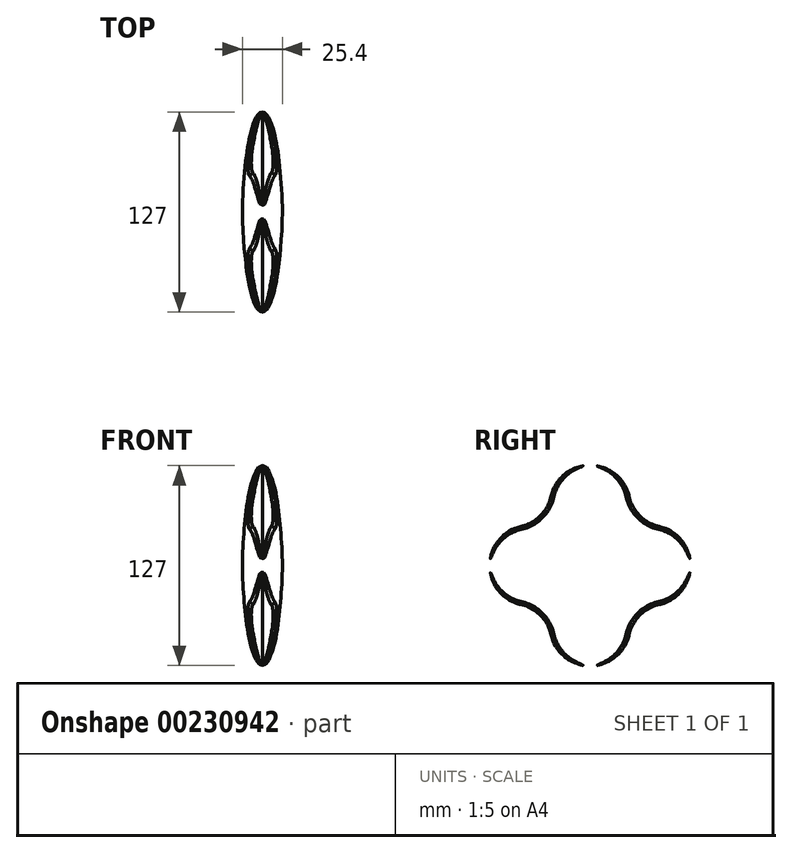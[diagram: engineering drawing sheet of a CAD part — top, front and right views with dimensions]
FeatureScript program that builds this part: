
annotation { "Feature Type Name" : "Feature", "Feature Type Description" : "" }
export const myFeature = defineFeature(function(context is Context, id is Id, definition is map)
    precondition{}
    {
        {
            var Q0;
            Q0=qCreatedBy(makeId("Top.planeOp"),FACE);
            var sketch = newSketch(context, id + "F0", { "sketchPlane" : qUnion([Q0])});
            skLineSegment(sketch, "E0", {"start": v(-58.3, 0) * mm, "end": v(61.26, 0) * mm, "construction": true});
            skLineSegment(sketch, "E1.bottom", {"start": v(0, 0) * mm, "end": v(-12.7, 0) * mm, "construction": true});
            skLineSegment(sketch, "E1.top", {"start": v(0, 63.5) * mm, "end": v(-12.7, 63.5) * mm, "construction": true});
            skLineSegment(sketch, "E1.left", {"start": v(0, 0) * mm, "end": v(0, 63.5) * mm, "construction": true});
            skLineSegment(sketch, "E1.right", {"start": v(-12.7, 0) * mm, "end": v(-12.7, 63.5) * mm, "construction": true});
            skPoint(sketch, "E2.2.internal.snap0", {"position": v(-6.35, 0) * mm});
            skFitSpline(sketch, "E2", {"points": [v(-12.7, 0) * mm, v(-10.15, 35.67) * mm, v(-6.35, 54.34) * mm, v(0, 63.5) * mm], "startDerivative": vector(0, 78.54) * mm, "endDerivative": vector(35.42, 0) * mm});
            skLineSegment(sketch, "E3", {"start": v(-12.7, 0) * mm, "end": v(0, 0) * mm});
            skLineSegment(sketch, "E4.MirrorCS", {"start": v(12.7, 0) * mm, "end": v(0, 0) * mm});
            skFitSpline(sketch, "E5.MirrorCS", {"points": [v(12.7, 0) * mm, v(10.15, 35.67) * mm, v(6.35, 54.34) * mm, v(0, 63.5) * mm], "startDerivative": vector(0, 78.54) * mm, "endDerivative": vector(-35.42, 0) * mm});
            skSolve(sketch);
        }
        {
            var Q0;
            Q0 = qSketchRegion(id + "F0", true);
            var Q1;
            Q1=sQuery(id+"F0.wireOp",EDGE,"E0");
            revolve(context, id + "F1", {"entities" : qUnion([Q0]), "axis" : qUnion([Q1]), "revolveType" : RevolveType.FULL});
        }
        {
            var Q0;
            Q0=qCreatedBy(makeId("Right.planeOp"),FACE);
            var sketch = newSketch(context, id + "F2", { "sketchPlane" : qUnion([Q0])});
            skLineSegment(sketch, "E6", {"start": v(68.88, 0) * mm, "end": v(-71.01, 0) * mm, "construction": true});
            skLineSegment(sketch, "E7", {"start": v(0, 73.64) * mm, "end": v(0, -72.57) * mm, "construction": true});
            skArc(sketch, "E8", {"start": v(43.95, -24.78) * mm, "mid": v(63.75, 0) * mm, "end": v(43.95, 24.78) * mm});
            skArc(sketch, "E9.1.0", {"start": v(24.78, 43.95) * mm, "mid": v(0, 63.75) * mm, "end": v(-24.78, 43.95) * mm});
            skArc(sketch, "E9.2.0", {"start": v(-43.95, 24.78) * mm, "mid": v(-63.75, 0) * mm, "end": v(-43.95, -24.78) * mm});
            skArc(sketch, "E9.3.0", {"start": v(-24.78, -43.95) * mm, "mid": v(0, -63.75) * mm, "end": v(24.78, -43.95) * mm});
            skPoint(sketch, "E9.center", {"position": v(0, 0) * mm});
            skArc(sketch, "E10", {"start": v(-43.95, 24.78) * mm, "mid": v(-31.6, 31.6) * mm, "end": v(-24.78, 43.95) * mm});
            skPoint(sketch, "E10.first.point", {"position": v(-24.78, 43.95) * mm});
            skPoint(sketch, "E10.second.point", {"position": v(-43.95, 24.78) * mm});
            skPoint(sketch, "E10.third.point", {"position": v(-73.77, 57.21) * mm});
            skArc(sketch, "E11.1.0", {"start": v(-24.78, -43.95) * mm, "mid": v(-31.6, -31.6) * mm, "end": v(-43.95, -24.78) * mm});
            skArc(sketch, "E11.2.0", {"start": v(43.95, -24.78) * mm, "mid": v(31.6, -31.6) * mm, "end": v(24.78, -43.95) * mm});
            skArc(sketch, "E11.3.0", {"start": v(24.78, 43.95) * mm, "mid": v(31.6, 31.6) * mm, "end": v(43.95, 24.78) * mm});
            skCircle(sketch, "E12", {"center": v(0, 0) * mm, "radius": 80.73 * mm});
            skCircle(sketch, "E13.0", {"center": v(0, 0) * mm, "radius": 63.75 * mm, "construction": true});
            skSolve(sketch);
        }
        {
            var Q0;
            Q0 = qSketchRegion(id + "F2", true);
            extrude(context, id + "F3", {"entities" : qUnion([Q0]), "operationType" : NewBodyOperationType.REMOVE, "endBound" : BoundingType.THROUGH_ALL, "oppositeDirection" : true, "depth" : 25.4 * mm, "hasDraft" : true, "draftAngle" : 3 * degree, "hasSecondDirection" : true, "secondDirectionBound" : SecondDirectionBoundingType.THROUGH_ALL, "secondDirectionOppositeDirection" : false, "secondDirectionDepth" : 25.4 * mm});
        }
        {
            var Q0;
            Q0=makeQuery(id+"F1.opRevolve","SWEPT_FACE",FACE,{"disambiguationData":[OSD([sQuery(id+"F0.wireOp",EDGE,"E5.MirrorCS")])]});
            var Q1;
            Q1=makeQuery(id+"F1.opRevolve","SWEPT_FACE",FACE,{"disambiguationData":[OSD([sQuery(id+"F0.wireOp",EDGE,"E2")])]});
            fillet(context, id + "F4", {"entities" : qUnion([Q0, Q1]), "radius" : 2.3 * mm, "tangentPropagation" : true, "rho" : 0.5, "crossSection" : FilletCrossSection.CONIC, "allowEdgeOverflow" : false});
        }
    });
